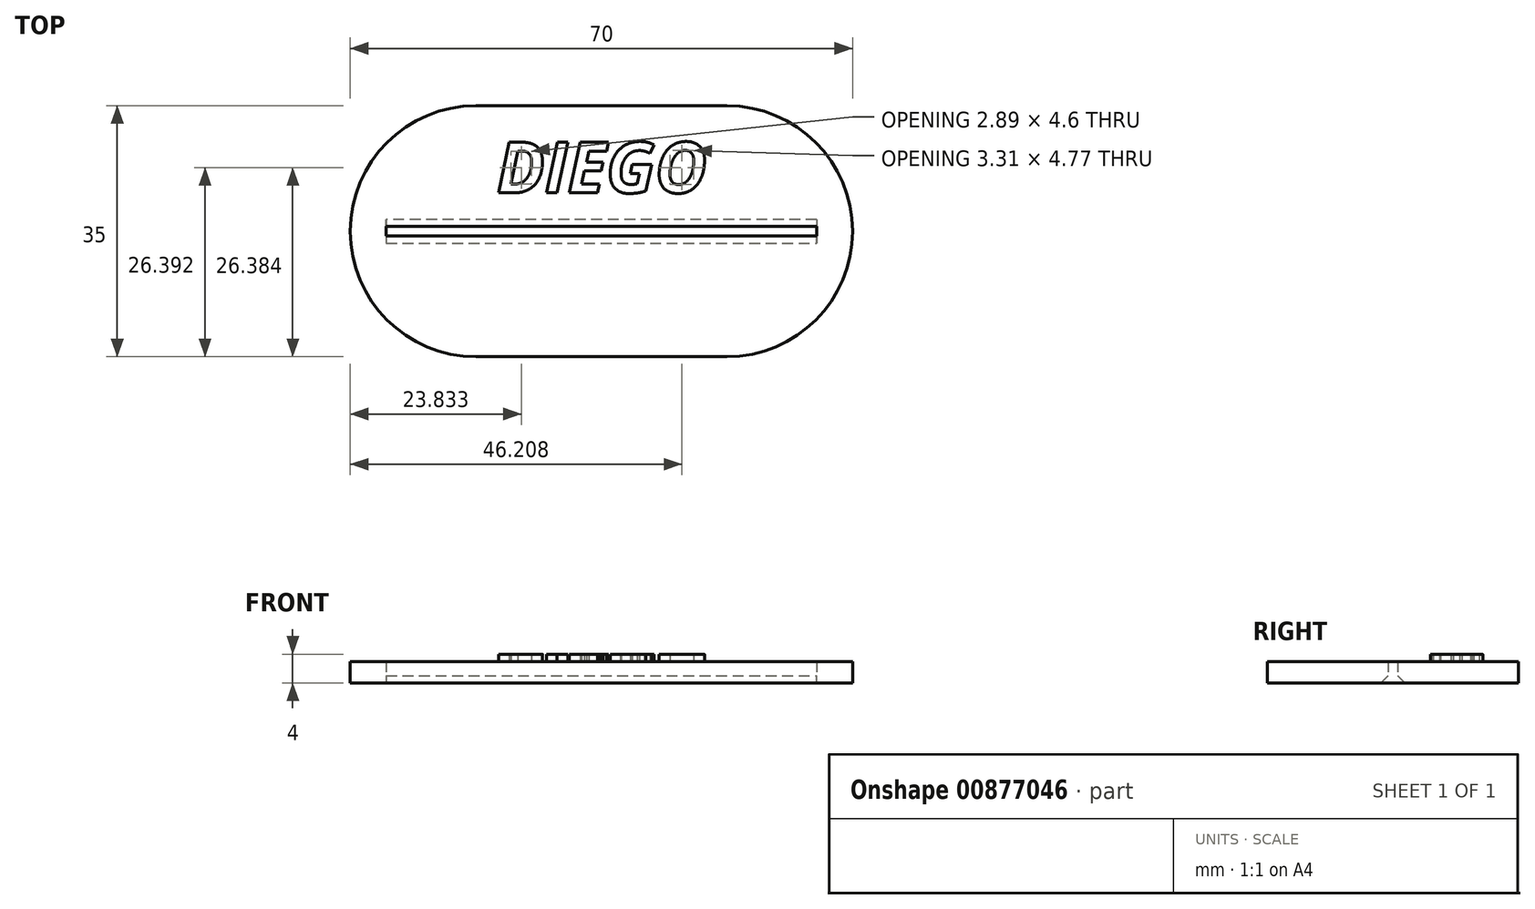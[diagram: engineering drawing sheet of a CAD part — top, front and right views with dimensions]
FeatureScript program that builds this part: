
annotation { "Feature Type Name" : "Feature", "Feature Type Description" : "" }
export const myFeature = defineFeature(function(context is Context, id is Id, definition is map)
    precondition{}
    {
        {
            var Q0;
            Q0=qCreatedBy(makeId("Top.planeOp"),FACE);
            var sketch = newSketch(context, id + "F0", { "sketchPlane" : qUnion([Q0])});
            skLineSegment(sketch, "E0.bottom", {"start": v(0, 0) * mm, "end": v(70, 0) * mm});
            skLineSegment(sketch, "E0.top", {"start": v(0, 35) * mm, "end": v(70, 35) * mm});
            skLineSegment(sketch, "E0.left", {"start": v(0, 0) * mm, "end": v(0, 35) * mm});
            skLineSegment(sketch, "E0.right", {"start": v(70, 0) * mm, "end": v(70, 35) * mm});
            skLineSegment(sketch, "E1.bottom", {"start": v(5, 18.15) * mm, "end": v(65, 18.15) * mm});
            skLineSegment(sketch, "E1.top", {"start": v(5, 16.85) * mm, "end": v(65, 16.85) * mm});
            skLineSegment(sketch, "E1.left", {"start": v(5, 18.15) * mm, "end": v(5, 16.85) * mm});
            skLineSegment(sketch, "E1.right", {"start": v(65, 18.15) * mm, "end": v(65, 16.85) * mm});
            skSolve(sketch);
        }
        {
            var Q0;
            Q0=qSketchRegion(id+"F0",true);
            extrude(context, id + "F1", {"entities" : qUnion([Q0]), "depth" : 3 * mm, "offsetDistance" : 25 * mm});
        }
        {
            var Q0;
            Q0=makeQuery(id+"F1.opExtrude","SWEPT_EDGE",EDGE,{"disambiguationData":[OSD([sQuery(id+"F0.wireOp",EDGE,"E0.bottom"),sQuery(id+"F0.wireOp",EDGE,"E0.right")])]});
            var Q1;
            Q1=makeQuery(id+"F1.opExtrude","SWEPT_EDGE",EDGE,{"disambiguationData":[OSD([sQuery(id+"F0.wireOp",EDGE,"E0.top"),sQuery(id+"F0.wireOp",EDGE,"E0.right")])]});
            var Q2;
            Q2=makeQuery(id+"F1.opExtrude","SWEPT_EDGE",EDGE,{"disambiguationData":[OSD([sQuery(id+"F0.wireOp",EDGE,"E0.top"),sQuery(id+"F0.wireOp",EDGE,"E0.left")])]});
            var Q3;
            Q3=makeQuery(id+"F1.opExtrude","SWEPT_EDGE",EDGE,{"disambiguationData":[OSD([sQuery(id+"F0.wireOp",EDGE,"E0.bottom"),sQuery(id+"F0.wireOp",EDGE,"E0.left")])]});
            fillet(context, id + "F2", {"entities" : qUnion([Q0, Q1, Q2, Q3]), "radius" : 17.5 * mm, "tangentPropagation" : true, "allowEdgeOverflow" : false});
        }
        {
            var Q0;
            Q0=makeQuery(id+"F1.opExtrude","CAP_EDGE",EDGE,{"disambiguationData":[OSD([sQuery(id+"F0.wireOp",EDGE,"E1.top")])],"isStart":true});
            var Q1;
            Q1=makeQuery(id+"F1.opExtrude","CAP_EDGE",EDGE,{"disambiguationData":[OSD([sQuery(id+"F0.wireOp",EDGE,"E1.bottom")])],"isStart":true});
            chamfer(context, id + "F3", {"entities" : qUnion([Q0, Q1]), "width" : 1 * mm, "tangentPropagation" : true});
        }
        {
            var Q0;
            Q0=makeQuery(id+"F1.opExtrude","CAP_FACE",FACE,{"disambiguationData":[OSD([sQuery(id+"F0.wireOp",EDGE,"E0.bottom"),sQuery(id+"F0.wireOp",EDGE,"E0.top"),sQuery(id+"F0.wireOp",EDGE,"E0.left"),sQuery(id+"F0.wireOp",EDGE,"E0.right"),sQuery(id+"F0.wireOp",EDGE,"E1.bottom"),sQuery(id+"F0.wireOp",EDGE,"E1.top"),sQuery(id+"F0.wireOp",EDGE,"E1.left"),sQuery(id+"F0.wireOp",EDGE,"E1.right")])],"isStart":false});
            var sketch = newSketch(context, id + "F4", { "sketchPlane" : qUnion([Q0])});
            skText(sketch, "E2", { "text": "DIEGO", "fontName": "OpenSans-BoldItalic.ttf"});
            const initialGuessF4  = {"E2": [0.0204, 0.02285, 1, 0, 0.00712]};
            skSetInitialGuess(sketch, initialGuessF4);
            skSolve(sketch);
        }
        {
            var Q0;
            Q0=qSketchRegion(id+"F4",true);
            extrude(context, id + "F5", {"entities" : qUnion([Q0]), "depth" : 1 * mm, "offsetDistance" : 25 * mm});
        }
    });
